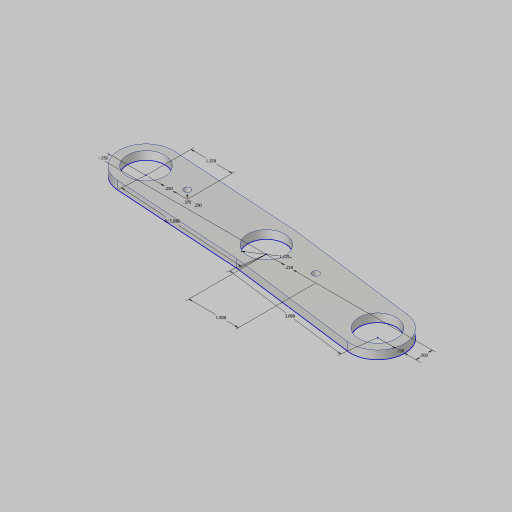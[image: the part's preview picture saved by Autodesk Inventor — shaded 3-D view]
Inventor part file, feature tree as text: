
AUTODESK INVENTOR PART (.ipt)
format: ipt  version: 2023.5 (Build 275446000, 446)  size: 122,368 bytes
history: native  units: in
note: dims shown in document units (in); Inventor stores cm internally (conversion verified against a paired STEP export)
features: sketch x1, extrude x1, hole x1
ambient origin geometry x8: Origin, YZ Plane, XZ Plane, XY Plane, X Axis, Y Axis, Z Axis, Center Point
bodies: Solid1 (feature_tree)
feature tree (3):
  sketch  "Sketch1"  dims[d0=1.125in d1=3.8976in d2=3.8976in d3=0.5in d4=0.25in d5=0.25in d6=0.25in d7=0.25in d8=1.25in d9=1.5in d10=0.375in d11=0.25in d12=0.25in d13=0.0in d14=0.201in d15=0.75in d16=0.385in d17=0.25in d18=0.5635in d19=1.0in d20=0.8108in]
  extrude  "Extrusion1"  Depth=3.8976in
  hole  "Hole1"  [1 undecoded]
note: 1 required parameter value undecoded (feature->parameter linkage not recoverable at this tier; creation-order binding heuristic only, values carry confidence <= 0.55)
